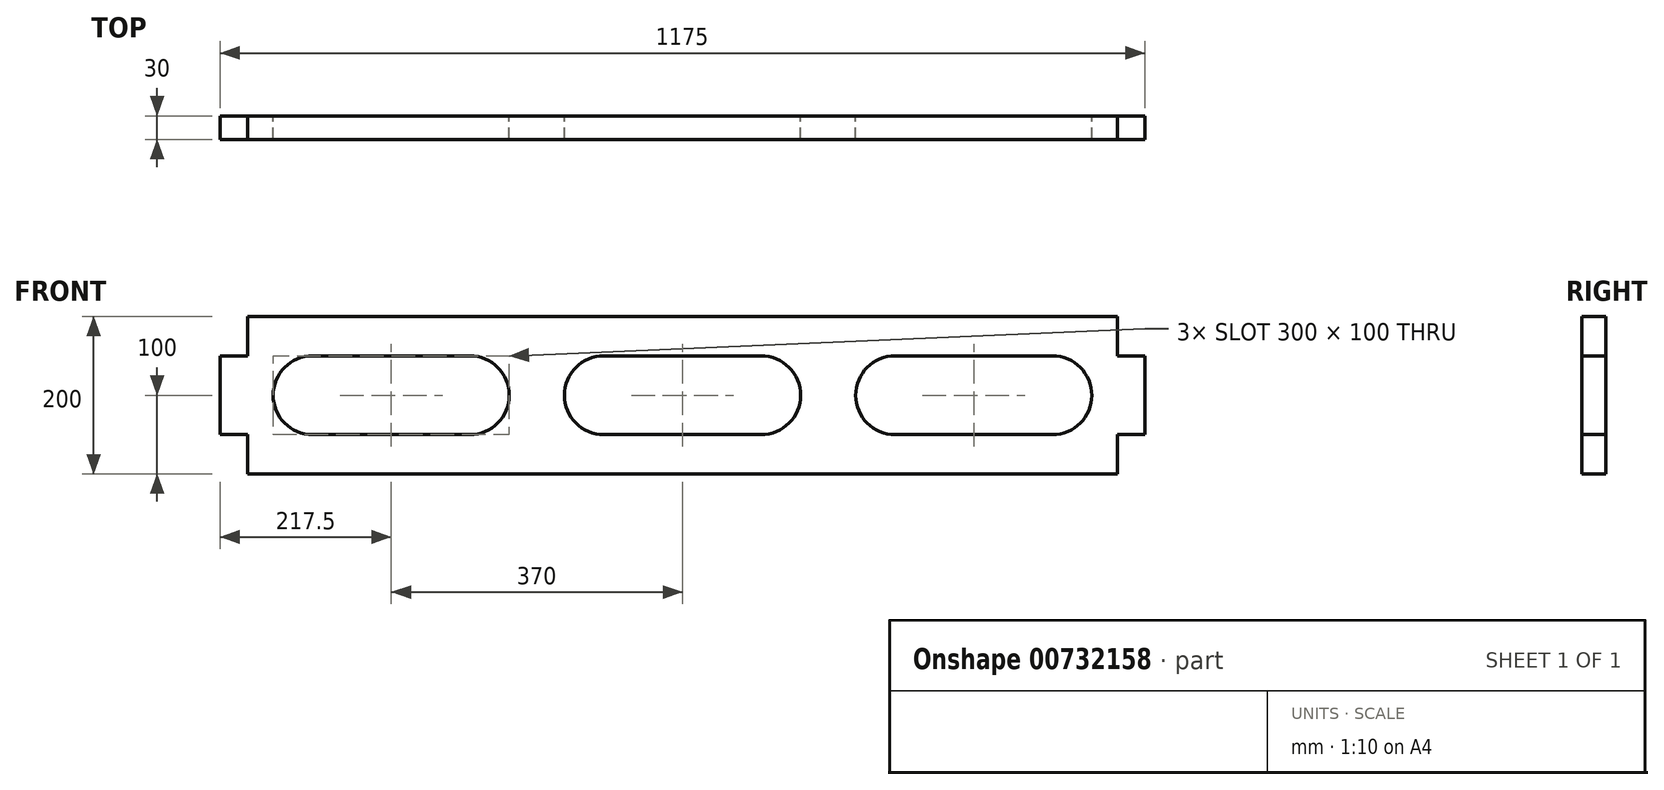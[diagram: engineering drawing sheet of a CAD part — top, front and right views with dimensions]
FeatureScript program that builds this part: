
annotation { "Feature Type Name" : "Feature", "Feature Type Description" : "" }
export const myFeature = defineFeature(function(context is Context, id is Id, definition is map)
    precondition{}
    {
        {
            var Q0;
            Q0=qCreatedBy(makeId("Front.planeOp"),FACE);
            var sketch = newSketch(context, id + "F0", { "sketchPlane" : qUnion([Q0])});
            skLineSegment(sketch, "E0.bottom", {"start": v(30, 0) * mm, "end": v(1135, 0) * mm});
            skLineSegment(sketch, "E0.top", {"start": v(30, 200) * mm, "end": v(1135, 200) * mm});
            skLineSegment(sketch, "E0.left", {"start": v(-5, 50) * mm, "end": v(-5, 150) * mm});
            skLineSegment(sketch, "E0.right", {"start": v(1170, 50) * mm, "end": v(1170, 150) * mm});
            skLineSegment(sketch, "E1.right", {"start": v(30, 0) * mm, "end": v(30, 50) * mm});
            skLineSegment(sketch, "E2.right", {"start": v(1135, 0) * mm, "end": v(1135, 50) * mm});
            skLineSegment(sketch, "E3.bottom", {"start": v(30, 150) * mm, "end": v(-5, 150) * mm});
            skLineSegment(sketch, "E3.top", {"start": v(30, 50) * mm, "end": v(-5, 50) * mm});
            skLineSegment(sketch, "E4.bottom", {"start": v(1135, 150) * mm, "end": v(1170, 150) * mm});
            skLineSegment(sketch, "E4.top", {"start": v(1135, 50) * mm, "end": v(1170, 50) * mm});
            skLineSegment(sketch, "E5.trimOffspring", {"start": v(30, 150) * mm, "end": v(30, 200) * mm});
            skLineSegment(sketch, "E6.trimOffspring", {"start": v(1135, 150) * mm, "end": v(1135, 200) * mm});
            skLineSegment(sketch, "E7.bottom", {"start": v(112.5, 50) * mm, "end": v(312.5, 50) * mm});
            skLineSegment(sketch, "E7.top", {"start": v(112.5, 150) * mm, "end": v(312.5, 150) * mm});
            skArc(sketch, "E8", {"start": v(112.5, 150) * mm, "mid": v(62.5, 100) * mm, "end": v(112.5, 50) * mm});
            skPoint(sketch, "E8.third.point", {"position": v(62.73, 104.76) * mm});
            skArc(sketch, "E9", {"start": v(312.5, 50) * mm, "mid": v(362.5, 100) * mm, "end": v(312.5, 150) * mm});
            skPoint(sketch, "E9.third.point", {"position": v(361.87, 107.92) * mm});
            skLineSegment(sketch, "E10.1.0.0", {"start": v(482.5, 50) * mm, "end": v(682.5, 50) * mm});
            skArc(sketch, "E10.1.0.1", {"start": v(482.5, 150) * mm, "mid": v(432.5, 100) * mm, "end": v(482.5, 50) * mm});
            skLineSegment(sketch, "E10.1.0.2", {"start": v(482.5, 150) * mm, "end": v(682.5, 150) * mm});
            skArc(sketch, "E10.1.0.3", {"start": v(682.5, 50) * mm, "mid": v(732.5, 100) * mm, "end": v(682.5, 150) * mm});
            skLineSegment(sketch, "E10.2.0.0", {"start": v(852.5, 50) * mm, "end": v(1052.5, 50) * mm});
            skArc(sketch, "E10.2.0.1", {"start": v(852.5, 150) * mm, "mid": v(802.5, 100) * mm, "end": v(852.5, 50) * mm});
            skLineSegment(sketch, "E10.2.0.2", {"start": v(852.5, 150) * mm, "end": v(1052.5, 150) * mm});
            skArc(sketch, "E10.2.0.3", {"start": v(1052.5, 50) * mm, "mid": v(1102.5, 100) * mm, "end": v(1052.5, 150) * mm});
            skLineSegment(sketch, "E10.direction1", {"start": v(112.5, 50) * mm, "end": v(482.5, 50) * mm, "construction": true});
            skSolve(sketch);
        }
        {
            var Q0;
            Q0=makeQuery(id+"F0.imprint","IMPRINT",FACE,{"disambiguationData":[TD([[makeQuery(id+"F0.imprint","IMPRINT",EDGE,{"derivedFrom":sQuery(id+"F0.wireOp",EDGE,"E0.bottom")}),1.0]])]});
            extrude(context, id + "F1", {"entities" : qUnion([Q0]), "depth" : 30 * mm, "offsetDistance" : 25 * mm});
        }
    });
